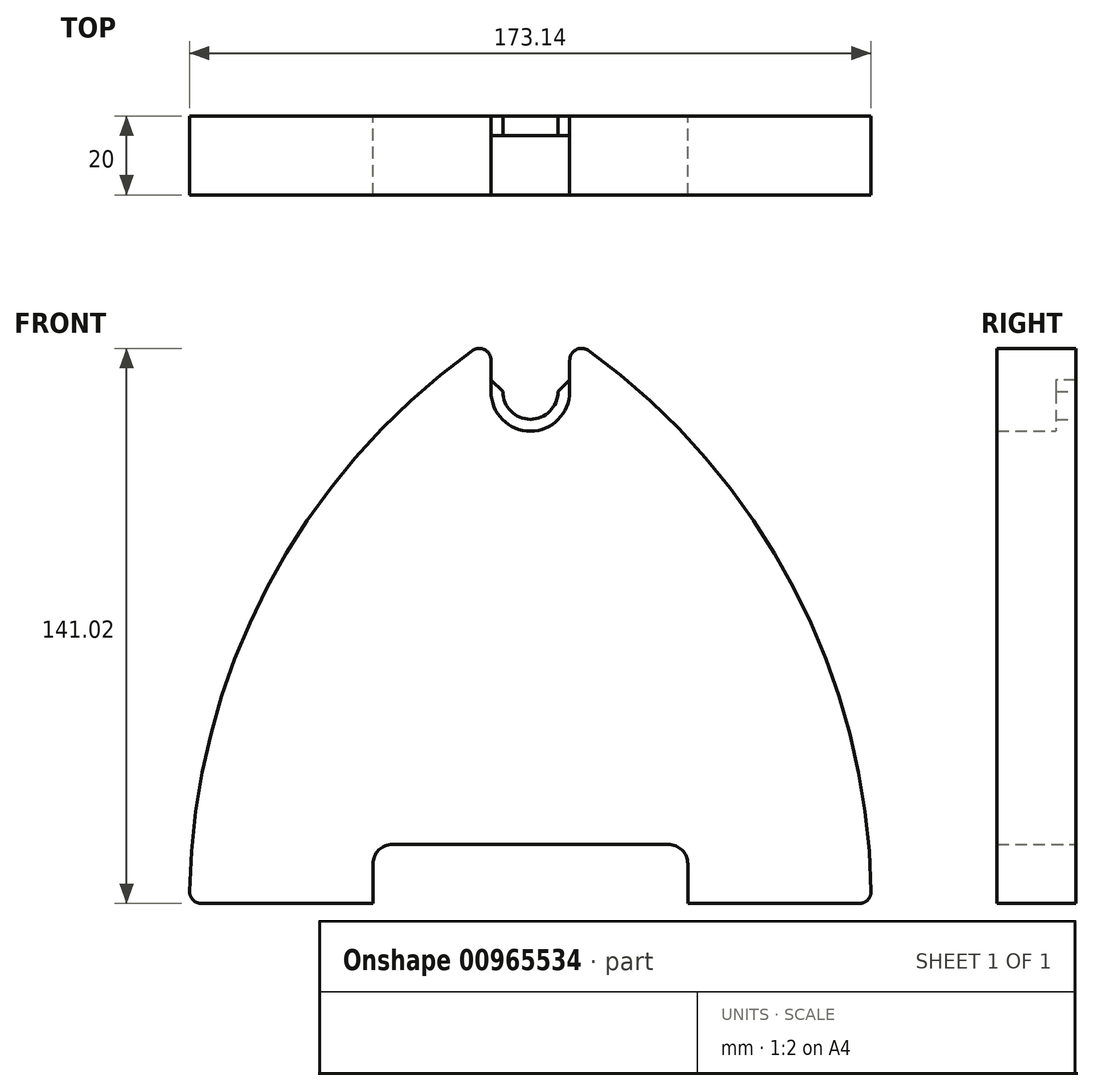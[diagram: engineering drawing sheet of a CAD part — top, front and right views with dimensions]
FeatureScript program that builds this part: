
annotation { "Feature Type Name" : "Feature", "Feature Type Description" : "" }
export const myFeature = defineFeature(function(context is Context, id is Id, definition is map)
    precondition{}
    {
        {
            var Q0;
            Q0=qCreatedBy(makeId("Front.planeOp"),FACE);
            var sketch = newSketch(context, id + "F0", { "sketchPlane" : qUnion([Q0])});
            skCircle(sketch, "E0.cCircle", {"center": v(0, 0) * mm, "radius": 100 * mm, "construction": true});
            skLineSegment(sketch, "E0.0", {"start": v(0, 100) * mm, "end": v(86.6, -50) * mm, "construction": true});
            skLineSegment(sketch, "E0.1", {"start": v(86.6, -50) * mm, "end": v(-86.6, -50) * mm});
            skLineSegment(sketch, "E0.2", {"start": v(-86.6, -50) * mm, "end": v(0, 100) * mm, "construction": true});
            skArc(sketch, "E1", {"start": v(0, 100) * mm, "mid": v(-5.05, 96.97) * mm, "end": v(-10, 93.76) * mm, "construction": true});
            skArc(sketch, "E2", {"start": v(86.6, -50) * mm, "mid": v(66.26, 31.45) * mm, "end": v(10, 93.76) * mm});
            skArc(sketch, "E3.0", {"start": v(70.89, -35) * mm, "mid": v(54.38, 21.8) * mm, "end": v(18.16, 68.55) * mm});
            skLineSegment(sketch, "E3.1", {"start": v(70.89, -35) * mm, "end": v(-70.89, -35) * mm});
            skArc(sketch, "E3.2", {"start": v(-18.16, 68.55) * mm, "mid": v(-54.38, 21.8) * mm, "end": v(-70.89, -35) * mm});
            skLineSegment(sketch, "E4", {"start": v(-10, 93.76) * mm, "end": v(-10, 80) * mm});
            skLineSegment(sketch, "E5", {"start": v(10, 93.76) * mm, "end": v(10, 80) * mm});
            skArc(sketch, "E6", {"start": v(-10, 80) * mm, "mid": v(0, 70) * mm, "end": v(10, 80) * mm});
            skArc(sketch, "E7", {"start": v(-10, 93.76) * mm, "mid": v(-66.26, 31.45) * mm, "end": v(-86.6, -50) * mm});
            skArc(sketch, "E8", {"start": v(10, 93.76) * mm, "mid": v(5.05, 96.97) * mm, "end": v(0, 100) * mm, "construction": true});
            skArc(sketch, "E9.0", {"start": v(-20.81, 66.15) * mm, "mid": v(0, 55) * mm, "end": v(20.81, 66.15) * mm});
            skArc(sketch, "E10.0", {"start": v(-7, 80) * mm, "mid": v(0, 73) * mm, "end": v(7, 80) * mm});
            skLineSegment(sketch, "E11", {"start": v(-7, 80) * mm, "end": v(-10, 80) * mm});
            skLineSegment(sketch, "E12", {"start": v(7, 80) * mm, "end": v(10, 80) * mm});
            skPoint(sketch, "E13", {"position": v(0, 70) * mm});
            skSolve(sketch);
        }
        {
            var Q0;
            Q0=makeQuery(id+"F0.imprint","IMPRINT",FACE,{"disambiguationData":[TD([[makeQuery(id+"F0.imprint","IMPRINT",EDGE,{"derivedFrom":sQuery(id+"F0.wireOp",EDGE,"E0.1")}),-1.0]])]});
            extrude(context, id + "F1", {"entities" : qUnion([Q0]), "depth" : 20 * mm, "offsetDistance" : 25 * mm});
        }
        {
            var Q0;
            Q0=makeQuery(id+"F0.imprint","IMPRINT",FACE,{"disambiguationData":[TD([[makeQuery(id+"F0.imprint","IMPRINT",EDGE,{"derivedFrom":sQuery(id+"F0.wireOp",EDGE,"E6")}),1.0]])]});
            extrude(context, id + "F2", {"entities" : qUnion([Q0]), "operationType" : NewBodyOperationType.ADD, "depth" : 5 * mm, "offsetDistance" : 25 * mm});
        }
        {
            var Q0;
            Q0=makeQuery(id+"F1.opExtrude","CAP_FACE",FACE,{"disambiguationData":[OSD([sQuery(id+"F0.wireOp",EDGE,"E0.1"),sQuery(id+"F0.wireOp",EDGE,"E2"),sQuery(id+"F0.wireOp",EDGE,"E3.0"),sQuery(id+"F0.wireOp",EDGE,"E3.1"),sQuery(id+"F0.wireOp",EDGE,"E3.2"),sQuery(id+"F0.wireOp",EDGE,"E4"),sQuery(id+"F0.wireOp",EDGE,"E5"),sQuery(id+"F0.wireOp",EDGE,"E6"),sQuery(id+"F0.wireOp",EDGE,"E7"),sQuery(id+"F0.wireOp",EDGE,"E9.0")])],"isStart":false});
            cPlane(context, id + "F3", {"entities" : qUnion([Q0]), "cplaneType" : CPlaneType.OFFSET, "offset" : 10 * mm, "oppositeDirection" : true, "width" : 150 * mm, "height" : 150 * mm});
        }
        {
            var Q0;
            Q0=makeQuery(id+"F1.opExtrude","SWEPT_EDGE",EDGE,{"disambiguationData":[OSD([sQuery(id+"F0.wireOp",EDGE,"E4"),sQuery(id+"F0.wireOp",EDGE,"E7")])]});
            var Q1;
            Q1=makeQuery(id+"F1.opExtrude","SWEPT_EDGE",EDGE,{"disambiguationData":[OSD([sQuery(id+"F0.wireOp",EDGE,"E2"),sQuery(id+"F0.wireOp",EDGE,"E5")])]});
            var Q2;
            Q2=makeQuery(id+"F1.opExtrude","SWEPT_EDGE",EDGE,{"disambiguationData":[OSD([sQuery(id+"F0.wireOp",EDGE,"E0.1"),sQuery(id+"F0.wireOp",EDGE,"E2")])]});
            var Q3;
            Q3=makeQuery(id+"F1.opExtrude","SWEPT_EDGE",EDGE,{"disambiguationData":[OSD([sQuery(id+"F0.wireOp",EDGE,"E0.1"),sQuery(id+"F0.wireOp",EDGE,"E7")])]});
            var Q4;
            Q4=makeQuery(id+"F1.opExtrude","SWEPT_EDGE",EDGE,{"disambiguationData":[OSD([sQuery(id+"F0.wireOp",EDGE,"E3.1"),sQuery(id+"F0.wireOp",EDGE,"E3.2")])]});
            var Q5;
            Q5=makeQuery(id+"F1.opExtrude","SWEPT_EDGE",EDGE,{"disambiguationData":[OSD([sQuery(id+"F0.wireOp",EDGE,"E3.0"),sQuery(id+"F0.wireOp",EDGE,"E3.1")])]});
            var Q6;
            Q6=makeQuery(id+"F1.opExtrude","SWEPT_EDGE",EDGE,{"disambiguationData":[OSD([sQuery(id+"F0.wireOp",EDGE,"E3.0"),sQuery(id+"F0.wireOp",EDGE,"E9.0")])]});
            var Q7;
            Q7=makeQuery(id+"F1.opExtrude","SWEPT_EDGE",EDGE,{"disambiguationData":[OSD([sQuery(id+"F0.wireOp",EDGE,"E3.2"),sQuery(id+"F0.wireOp",EDGE,"E9.0")])]});
            fillet(context, id + "F4", {"entities" : qUnion([Q0, Q1, Q2, Q3, Q4, Q5, Q6, Q7]), "radius" : 3 * mm, "tangentPropagation" : true, "allowEdgeOverflow" : false});
        }
        {
            var Q0;
            {var subQ0=sQuery(id+"F0.wireOp",EDGE,"E11");var subQ1=sQuery(id+"F0.wireOp",EDGE,"E6");var subQ2=sQuery(id+"F0.wireOp",EDGE,"E4");Q0=makeQuery(id+"F2.boolean.opBoolean","MERGE",EDGE,{"derivedFrom":[makeQuery(id+"F1.opExtrude","SWEPT_EDGE",EDGE,{"disambiguationData":[OSD([subQ2,subQ1,subQ0])]}),makeQuery(id+"F2.opExtrude","SWEPT_EDGE",EDGE,{"disambiguationData":[OSD([subQ2,subQ1,subQ0])]})]});}
            var Q1;
            {var subQ0=sQuery(id+"F0.wireOp",EDGE,"E11");var subQ1=sQuery(id+"F0.wireOp",EDGE,"E6");var subQ2=sQuery(id+"F0.wireOp",EDGE,"E4");Q1=makeQuery(id+"FTESzf3rQSRIyyg_1.1.F2.boolean.opBoolean","MERGE",EDGE,{"derivedFrom":[makeQuery(id+"F2.boolean.opBoolean","SPLIT",EDGE,{"derivedFrom":makeQuery(id+"F1.opExtrude","SWEPT_EDGE",EDGE,{"disambiguationData":[OSD([subQ2,subQ1,subQ0])]})}),makeQuery(id+"FTESzf3rQSRIyyg_1.1.F2.opExtrude","SWEPT_EDGE",EDGE,{"disambiguationData":[OSD([subQ2,subQ1,subQ0])]})]});}
            var Q2;
            {var subQ0=sQuery(id+"F0.wireOp",EDGE,"E12");var subQ1=sQuery(id+"F0.wireOp",EDGE,"E6");var subQ2=sQuery(id+"F0.wireOp",EDGE,"E5");Q2=makeQuery(id+"FTESzf3rQSRIyyg_1.1.F2.boolean.opBoolean","MERGE",EDGE,{"derivedFrom":[makeQuery(id+"F2.boolean.opBoolean","SPLIT",EDGE,{"derivedFrom":makeQuery(id+"F1.opExtrude","SWEPT_EDGE",EDGE,{"disambiguationData":[OSD([subQ2,subQ1,subQ0])]})}),makeQuery(id+"FTESzf3rQSRIyyg_1.1.F2.opExtrude","SWEPT_EDGE",EDGE,{"disambiguationData":[OSD([subQ2,subQ1,subQ0])]})]});}
            var Q3;
            {var subQ0=sQuery(id+"F0.wireOp",EDGE,"E12");var subQ1=sQuery(id+"F0.wireOp",EDGE,"E6");var subQ2=sQuery(id+"F0.wireOp",EDGE,"E5");Q3=makeQuery(id+"F2.boolean.opBoolean","MERGE",EDGE,{"derivedFrom":[makeQuery(id+"F1.opExtrude","SWEPT_EDGE",EDGE,{"disambiguationData":[OSD([subQ2,subQ1,subQ0])]}),makeQuery(id+"F2.opExtrude","SWEPT_EDGE",EDGE,{"disambiguationData":[OSD([subQ2,subQ1,subQ0])]})]});}
            chamfer(context, id + "F5", {"entities" : qUnion([Q0, Q1, Q2, Q3]), "width" : 3 * mm, "tangentPropagation" : true});
        }
        {
            var Q0;
            {var subQ0=sQuery(id+"F0.wireOp",EDGE,"E6");Q0=makeQuery(id+"F2.boolean.opBoolean","MERGE",FACE,{"derivedFrom":[makeQuery(id+"F1.opExtrude","CAP_FACE",FACE,{"disambiguationData":[OSD([sQuery(id+"F0.wireOp",EDGE,"E0.1"),sQuery(id+"F0.wireOp",EDGE,"E2"),sQuery(id+"F0.wireOp",EDGE,"E3.0"),sQuery(id+"F0.wireOp",EDGE,"E3.1"),sQuery(id+"F0.wireOp",EDGE,"E3.2"),sQuery(id+"F0.wireOp",EDGE,"E4"),sQuery(id+"F0.wireOp",EDGE,"E5"),subQ0,sQuery(id+"F0.wireOp",EDGE,"E7"),sQuery(id+"F0.wireOp",EDGE,"E9.0")])],"isStart":true}),makeQuery(id+"F2.opExtrude","CAP_FACE",FACE,{"disambiguationData":[OSD([subQ0,sQuery(id+"F0.wireOp",EDGE,"E10.0"),sQuery(id+"F0.wireOp",EDGE,"E11"),sQuery(id+"F0.wireOp",EDGE,"E12")])],"isStart":true})]});}
            var sketch = newSketch(context, id + "F6", { "sketchPlane" : qUnion([Q0])});
            skLineSegment(sketch, "E14.bottom", {"start": v(-40, -50) * mm, "end": v(40, -50) * mm});
            skLineSegment(sketch, "E14.top", {"start": v(-40, -35) * mm, "end": v(40, -35) * mm});
            skLineSegment(sketch, "E14.left", {"start": v(-40, -50) * mm, "end": v(-40, -35) * mm});
            skLineSegment(sketch, "E14.right", {"start": v(40, -50) * mm, "end": v(40, -35) * mm});
            skPoint(sketch, "E15", {"position": v(0, -35) * mm});
            skSolve(sketch);
        }
        {
            var Q0;
            Q0 = qSketchRegion(id + "F6", true);
            extrude(context, id + "F7", {"entities" : qUnion([Q0]), "operationType" : NewBodyOperationType.REMOVE, "endBound" : BoundingType.UP_TO_NEXT, "oppositeDirection" : true, "depth" : 25 * mm, "offsetDistance" : 25 * mm});
        }
        {
            var Q0;
            Q0=makeQuery(id+"F7.boolean.opBoolean","COPY",EDGE,{"derivedFrom":makeQuery(id+"F7.opExtrude","SWEPT_EDGE",EDGE,{"disambiguationData":[OSD([sQuery(id+"F0.wireOp",EDGE,"E3.1"),sQuery(id+"F6.wireOp",EDGE,"E14.top"),sQuery(id+"F6.wireOp",EDGE,"E14.left")])]})});
            var Q1;
            Q1=makeQuery(id+"F7.boolean.opBoolean","COPY",EDGE,{"derivedFrom":makeQuery(id+"F7.opExtrude","SWEPT_EDGE",EDGE,{"disambiguationData":[OSD([sQuery(id+"F0.wireOp",EDGE,"E3.1"),sQuery(id+"F6.wireOp",EDGE,"E14.top"),sQuery(id+"F6.wireOp",EDGE,"E14.right")])]})});
            fillet(context, id + "F8", {"entities" : qUnion([Q0, Q1]), "radius" : 5 * mm, "tangentPropagation" : true, "allowEdgeOverflow" : false});
        }
    });
